# Revit family: ZPT22
name_source: partatom
category: Lighting Fixtures
revit_build: Autodesk Revit Architecture 2012 (Build: 20110309_2315(x64)
units: mm (PartAtom-declared; Revit-internal decimal feet)

## types (16) — shared parameters
Backbox = White
Color Filter = 16777215
Default Elevation = 48.000"
Description = Zero Plenum® Troffer High Efficiency Architectural Luminaire
Dimming Lamp Color Temperature Shift = <None>
Emit Shape Visible in Rendering = No
Emit from Rectangle Length = 47.000"
Emit from Rectangle Width = 11.000"
Glass = Glass
Lamp = F28T8
Manufacturer = Columbia Lighting
Manufacturer Fax = 866-898-1065
Model = ZPT22
Product Documentation Link = http://www.columbialighting.com
Product Page URL = http://www.columbialighting.com
Tilt Angle = -90.00°
URL = http://www.columbialighting.com
Wattage Comments = 62 W

## per-type parameters (varying)
| type | Photometric Web File |
| ZPT22-214G-FCBO | 14314 |
| ZPT22-214G-FCBR | 14307 |
| ZPT22-214G-FCBS | 14304 |
| ZPT22-214G-LSRO | 14319 |
| ZPT22-214G-LSRR | 14032 |
| ZPT22-214G-LSRS | 14312 |
| ZPT22-214G-PRFR | 14301 |
| ZPT22-214G-PRFS | 14029 |
| ZPT22-224G-FCBO | 14313 |
| ZPT22-224G-FCBR | 14311 |
| ZPT22-224G-FCBS | 14310 |
| ZPT22-224G-LSRO | 14302 |
| ZPT22-224G-LSRR | 14026 |
| ZPT22-224G-PRFR | 14299 |
| ZPT22-224G-PRFS | 14030 |
| type_15 |  |

## geometry (parser evidence)
native form markers: Sweep x3
no freeform markers — native parametric forms only
